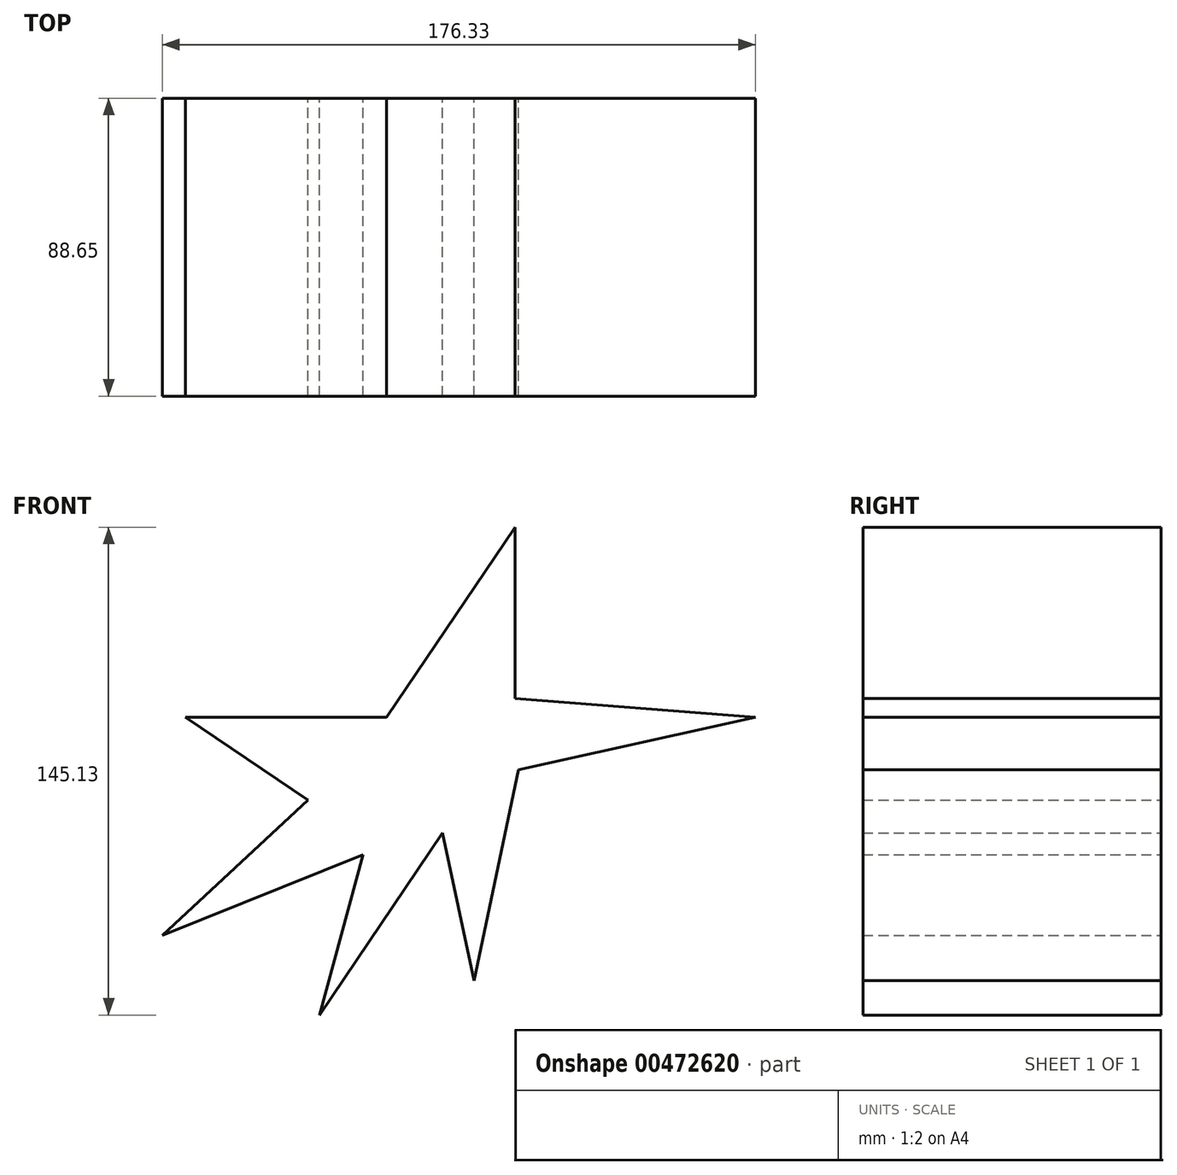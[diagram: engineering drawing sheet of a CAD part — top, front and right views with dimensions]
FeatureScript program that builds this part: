
annotation { "Feature Type Name" : "Feature", "Feature Type Description" : "" }
export const myFeature = defineFeature(function(context is Context, id is Id, definition is map)
    precondition{}
    {
        {
            var Q0;
            Q0=qCreatedBy(makeId("Front.planeOp"),FACE);
            var sketch = newSketch(context, id + "F0", { "sketchPlane" : qUnion([Q0])});
            skLineSegment(sketch, "E0", {"start": v(0, 0) * mm, "end": v(36.63, 54.2) * mm});
            skLineSegment(sketch, "E1", {"start": v(36.63, 54.2) * mm, "end": v(45.97, 10.22) * mm});
            skLineSegment(sketch, "E2", {"start": v(45.97, 10.22) * mm, "end": v(59.26, 72.95) * mm});
            skLineSegment(sketch, "E3", {"start": v(59.26, 72.95) * mm, "end": v(129.64, 88.6) * mm});
            skLineSegment(sketch, "E4", {"start": v(129.64, 88.6) * mm, "end": v(58.18, 94.19) * mm});
            skLineSegment(sketch, "E5", {"start": v(58.18, 94.19) * mm, "end": v(58.18, 145.13) * mm});
            skLineSegment(sketch, "E6", {"start": v(58.18, 145.13) * mm, "end": v(19.98, 88.6) * mm});
            skLineSegment(sketch, "E7", {"start": v(19.98, 88.6) * mm, "end": v(-39.86, 88.6) * mm});
            skLineSegment(sketch, "E8", {"start": v(-39.86, 88.6) * mm, "end": v(-3.39, 63.95) * mm});
            skLineSegment(sketch, "E9", {"start": v(-3.39, 63.95) * mm, "end": v(-46.69, 23.7) * mm});
            skLineSegment(sketch, "E10", {"start": v(-46.69, 23.7) * mm, "end": v(12.93, 47.73) * mm});
            skLineSegment(sketch, "E11", {"start": v(12.93, 47.73) * mm, "end": v(0, 0) * mm});
            skSolve(sketch);
        }
        {
            var Q0;
            Q0=makeQuery(id+"F0.imprint","IMPRINT",FACE,{"disambiguationData":[TD([[makeQuery(id+"F0.imprint","IMPRINT",EDGE,{"derivedFrom":sQuery(id+"F0.wireOp",EDGE,"E0")}),1.0]])]});
            extrude(context, id + "F1", {"entities" : qUnion([Q0]), "depth" : 88.65 * mm});
        }
    });
